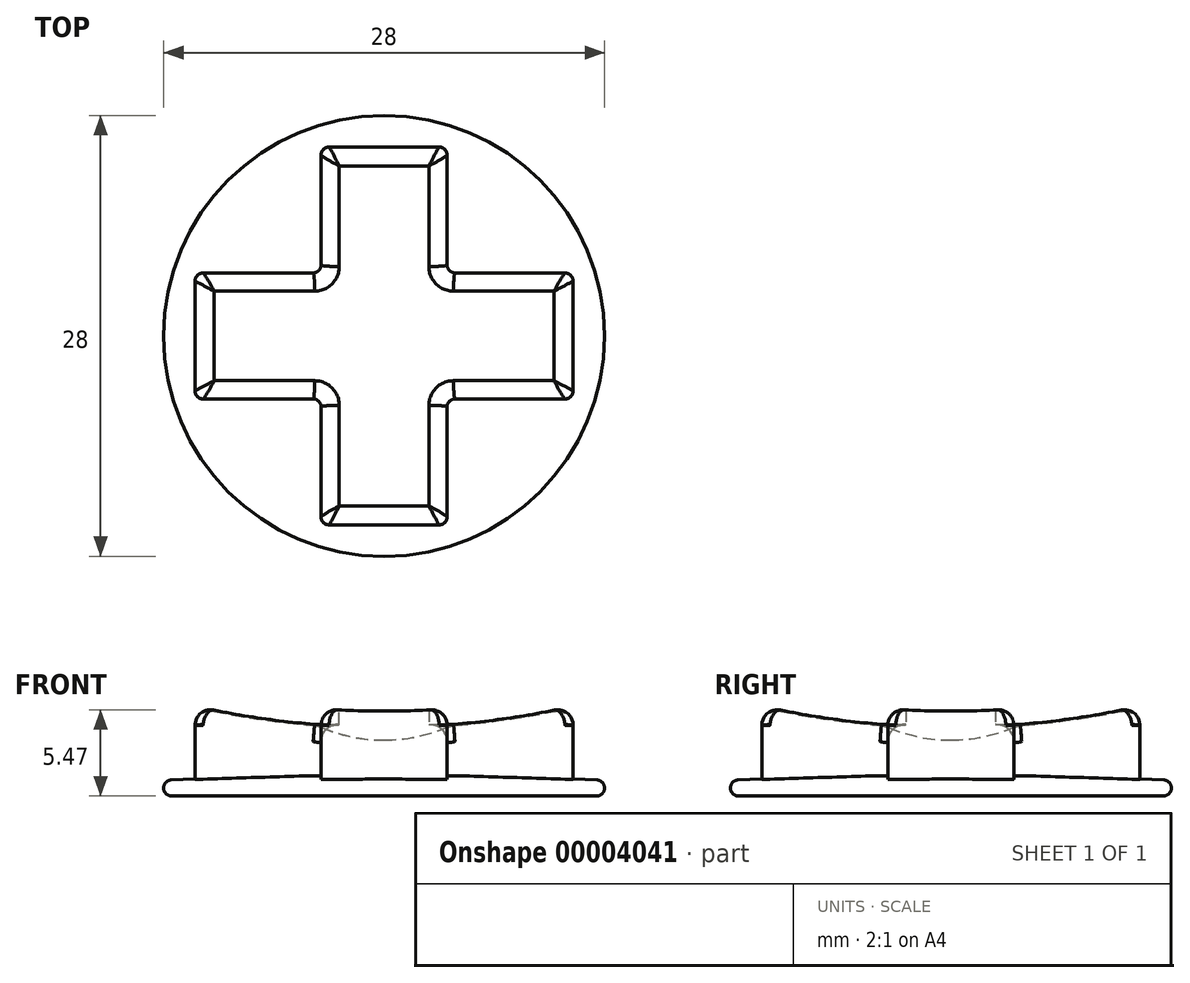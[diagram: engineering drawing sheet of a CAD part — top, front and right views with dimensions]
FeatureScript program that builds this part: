
annotation { "Feature Type Name" : "Feature", "Feature Type Description" : "" }
export const myFeature = defineFeature(function(context is Context, id is Id, definition is map)
    precondition{}
    {
        {
            var Q0;
            Q0=qCreatedBy(makeId("Top.planeOp"),FACE);
            var sketch = newSketch(context, id + "F0", { "sketchPlane" : qUnion([Q0])});
            skCircle(sketch, "E0", {"center": v(0, 0) * mm, "radius": 14 * mm});
            skSolve(sketch);
        }
        {
            var Q0;
            Q0=makeQuery(id+"F0.imprint","IMPRINT",FACE,{"disambiguationData":[TD([[makeQuery(id+"F0.imprint","IMPRINT",EDGE,{"derivedFrom":sQuery(id+"F0.wireOp",EDGE,"E0")}),1.0]])]});
            extrude(context, id + "F1", {"entities" : qUnion([Q0]), "depth" : 1 * mm});
        }
        {
            var Q0;
            Q0=makeQuery(id+"F1.opExtrude","CAP_FACE",FACE,{"disambiguationData":[OSD([sQuery(id+"F0.wireOp",EDGE,"E0")])],"isStart":false});
            var sketch = newSketch(context, id + "F2", { "sketchPlane" : qUnion([Q0])});
            skLineSegment(sketch, "E1", {"start": v(-4, 12) * mm, "end": v(0, 12) * mm});
            skLineSegment(sketch, "E2", {"start": v(0, 12) * mm, "end": v(4, 12) * mm});
            skLineSegment(sketch, "E3", {"start": v(4, 12) * mm, "end": v(4, 4) * mm});
            skLineSegment(sketch, "E4", {"start": v(4, 4) * mm, "end": v(12, 4) * mm});
            skLineSegment(sketch, "E5", {"start": v(12, 4) * mm, "end": v(12, 0) * mm});
            skLineSegment(sketch, "E6", {"start": v(12, 0) * mm, "end": v(12, -4) * mm});
            skLineSegment(sketch, "E7", {"start": v(12, -4) * mm, "end": v(4, -4) * mm});
            skLineSegment(sketch, "E8", {"start": v(4, -12) * mm, "end": v(0, -12) * mm});
            skLineSegment(sketch, "E9", {"start": v(0, -12) * mm, "end": v(-4, -12) * mm});
            skLineSegment(sketch, "E10", {"start": v(-4, -12) * mm, "end": v(-4, -4) * mm});
            skLineSegment(sketch, "E11", {"start": v(-4, -4) * mm, "end": v(-12, -4) * mm});
            skLineSegment(sketch, "E12", {"start": v(-12, -4) * mm, "end": v(-12, 0) * mm});
            skLineSegment(sketch, "E13", {"start": v(-12, 0) * mm, "end": v(-12, 4) * mm});
            skLineSegment(sketch, "E14", {"start": v(-12, 4) * mm, "end": v(-4, 4) * mm});
            skLineSegment(sketch, "E15", {"start": v(-4, 4) * mm, "end": v(-4, 12) * mm});
            skLineSegment(sketch, "E16", {"start": v(-4, 4) * mm, "end": v(0, 0) * mm, "construction": true});
            skLineSegment(sketch, "E17", {"start": v(0, 0) * mm, "end": v(4, 4) * mm, "construction": true});
            skLineSegment(sketch, "E18", {"start": v(0, 0) * mm, "end": v(4, -4) * mm, "construction": true});
            skLineSegment(sketch, "E19", {"start": v(0, 0) * mm, "end": v(-4, -4) * mm, "construction": true});
            skLineSegment(sketch, "E20", {"start": v(4, -4) * mm, "end": v(4, -12) * mm});
            skSolve(sketch);
        }
        {
            var Q0;
            Q0=makeQuery(id+"F2.imprint","IMPRINT",FACE,{"disambiguationData":[TD([[makeQuery(id+"F2.imprint","IMPRINT",EDGE,{"derivedFrom":sQuery(id+"F2.wireOp",EDGE,"E1")}),-1.0]])]});
            extrude(context, id + "F3", {"entities" : qUnion([Q0]), "operationType" : NewBodyOperationType.ADD, "depth" : 4.8 * mm});
        }
        {
            var Q0;
            Q0=qCreatedBy(makeId("Front.planeOp"),FACE);
            var sketch = newSketch(context, id + "F4", { "sketchPlane" : qUnion([Q0])});
            skLineSegment(sketch, "E21", {"start": v(0, 4.3) * mm, "end": v(0, 5.8) * mm});
            skLineSegment(sketch, "E22", {"start": v(0, 5.8) * mm, "end": v(-12.75, 5.8) * mm});
            skArc(sketch, "E23", {"start": v(-12.75, 5.8) * mm, "mid": v(-6.42, 4.68) * mm, "end": v(0, 4.3) * mm});
            skLineSegment(sketch, "E24", {"start": v(0, 4.3) * mm, "end": v(0, 3.55) * mm});
            skLineSegment(sketch, "E25", {"start": v(0, 3.55) * mm, "end": v(0, 0) * mm, "construction": true});
            skArc(sketch, "E26", {"start": v(-4.25, 4.46) * mm, "mid": v(-2.17, 3.78) * mm, "end": v(0, 3.55) * mm});
            skSolve(sketch);
        }
        {
            var Q0;
            {var subQ2=sQuery(id+"F4.wireOp",EDGE,"E21");Q0=makeQuery(id+"F4.imprint","IMPRINT",FACE,{"disambiguationData":[TD([[makeQuery(id+"F4.imprint","IMPRINT",EDGE,{"derivedFrom":subQ2}),1.0]])]});}
            var Q1;
            {var subQ1=sQuery(id+"F4.wireOp",EDGE,"E24");Q1=makeQuery(id+"F4.imprint","IMPRINT",FACE,{"disambiguationData":[TD([[makeQuery(id+"F4.imprint","IMPRINT",EDGE,{"derivedFrom":subQ1}),-1.0]])]});}
            var Q2;
            Q2=sQuery(id+"F4.wireOp",EDGE,"E24");
            revolve(context, id + "F5", {"operationType" : NewBodyOperationType.REMOVE, "entities" : qUnion([Q0, Q1]), "axis" : qUnion([Q2]), "revolveType" : RevolveType.FULL, "oppositeDirection" : true});
        }
        {
            var Q0;
            Q0=qCreatedBy(makeId("Front.planeOp"),FACE);
            var sketch = newSketch(context, id + "F6", { "sketchPlane" : qUnion([Q0])});
            skLineSegment(sketch, "E27.0", {"start": v(-14, 1) * mm, "end": v(14, 1) * mm});
            skLineSegment(sketch, "E28", {"start": v(0, 0) * mm, "end": v(0, 1) * mm, "construction": true});
            skLineSegment(sketch, "E29", {"start": v(0, 1) * mm, "end": v(0, 1.5) * mm});
            skLineSegment(sketch, "E30", {"start": v(0, 1.5) * mm, "end": v(-14, 1) * mm});
            skSolve(sketch);
        }
        {
            var Q0;
            {var subQ1=sQuery(id+"F6.wireOp",EDGE,"E29");Q0=makeQuery(id+"F6.imprint","IMPRINT",FACE,{"disambiguationData":[TD([[makeQuery(id+"F6.imprint","IMPRINT",EDGE,{"derivedFrom":subQ1}),1.0]])]});}
            var Q1;
            Q1=sQuery(id+"F6.wireOp",EDGE,"E29");
            revolve(context, id + "F7", {"operationType" : NewBodyOperationType.ADD, "entities" : qUnion([Q0]), "axis" : qUnion([Q1]), "revolveType" : RevolveType.FULL});
        }
        {
            var Q0;
            Q0=makeQuery(id+"F5.boolean.opBoolean","INTERSECT",EDGE,{"derivedFrom":[makeQuery(id+"F3.opExtrude","SWEPT_FACE",FACE,{"disambiguationData":[OSD([sQuery(id+"F2.wireOp",EDGE,"E8"),sQuery(id+"F2.wireOp",EDGE,"E9")])]}),makeQuery(id+"F5.opRevolve","SWEPT_FACE",FACE,{"disambiguationData":[OSD([sQuery(id+"F4.wireOp",EDGE,"E23")])]})]});
            var Q1;
            Q1=makeQuery(id+"F5.boolean.opBoolean","INTERSECT",EDGE,{"derivedFrom":[makeQuery(id+"F3.opExtrude","SWEPT_FACE",FACE,{"disambiguationData":[OSD([sQuery(id+"F2.wireOp",EDGE,"E12"),sQuery(id+"F2.wireOp",EDGE,"E13")])]}),makeQuery(id+"F5.opRevolve","SWEPT_FACE",FACE,{"disambiguationData":[OSD([sQuery(id+"F4.wireOp",EDGE,"E23")])]})]});
            var Q2;
            Q2=makeQuery(id+"F5.boolean.opBoolean","INTERSECT",EDGE,{"derivedFrom":[makeQuery(id+"F3.opExtrude","SWEPT_FACE",FACE,{"disambiguationData":[OSD([sQuery(id+"F2.wireOp",EDGE,"E5"),sQuery(id+"F2.wireOp",EDGE,"E6")])]}),makeQuery(id+"F5.opRevolve","SWEPT_FACE",FACE,{"disambiguationData":[OSD([sQuery(id+"F4.wireOp",EDGE,"E23")])]})]});
            var Q3;
            Q3=makeQuery(id+"F5.boolean.opBoolean","INTERSECT",EDGE,{"derivedFrom":[makeQuery(id+"F3.opExtrude","SWEPT_FACE",FACE,{"disambiguationData":[OSD([sQuery(id+"F2.wireOp",EDGE,"E1"),sQuery(id+"F2.wireOp",EDGE,"E2")])]}),makeQuery(id+"F5.opRevolve","SWEPT_FACE",FACE,{"disambiguationData":[OSD([sQuery(id+"F4.wireOp",EDGE,"E23")])]})]});
            fillet(context, id + "F8", {"entities" : qUnion([Q0, Q1, Q2, Q3]), "radius" : 1 * mm, "allowEdgeOverflow" : false});
        }
        {
            var Q0;
            Q0=makeQuery(id+"F3.opExtrude","SWEPT_EDGE",EDGE,{"disambiguationData":[OSD([sQuery(id+"F2.wireOp",EDGE,"E3"),sQuery(id+"F2.wireOp",EDGE,"E4")])]});
            var Q1;
            Q1=makeQuery(id+"F3.opExtrude","SWEPT_EDGE",EDGE,{"disambiguationData":[OSD([sQuery(id+"F2.wireOp",EDGE,"E4"),sQuery(id+"F2.wireOp",EDGE,"E5")])]});
            var Q2;
            Q2=makeQuery(id+"F3.opExtrude","SWEPT_EDGE",EDGE,{"disambiguationData":[OSD([sQuery(id+"F2.wireOp",EDGE,"E2"),sQuery(id+"F2.wireOp",EDGE,"E3")])]});
            var Q3;
            Q3=makeQuery(id+"F3.opExtrude","SWEPT_EDGE",EDGE,{"disambiguationData":[OSD([sQuery(id+"F2.wireOp",EDGE,"E1"),sQuery(id+"F2.wireOp",EDGE,"E15")])]});
            var Q4;
            Q4=makeQuery(id+"F3.opExtrude","SWEPT_EDGE",EDGE,{"disambiguationData":[OSD([sQuery(id+"F2.wireOp",EDGE,"E14"),sQuery(id+"F2.wireOp",EDGE,"E15")])]});
            var Q5;
            Q5=makeQuery(id+"F3.opExtrude","SWEPT_EDGE",EDGE,{"disambiguationData":[OSD([sQuery(id+"F2.wireOp",EDGE,"E13"),sQuery(id+"F2.wireOp",EDGE,"E14")])]});
            var Q6;
            Q6=makeQuery(id+"F3.opExtrude","SWEPT_EDGE",EDGE,{"disambiguationData":[OSD([sQuery(id+"F2.wireOp",EDGE,"E11"),sQuery(id+"F2.wireOp",EDGE,"E12")])]});
            var Q7;
            Q7=makeQuery(id+"F3.opExtrude","SWEPT_EDGE",EDGE,{"disambiguationData":[OSD([sQuery(id+"F2.wireOp",EDGE,"E10"),sQuery(id+"F2.wireOp",EDGE,"E11")])]});
            var Q8;
            Q8=makeQuery(id+"F3.opExtrude","SWEPT_EDGE",EDGE,{"disambiguationData":[OSD([sQuery(id+"F2.wireOp",EDGE,"E9"),sQuery(id+"F2.wireOp",EDGE,"E10")])]});
            var Q9;
            Q9=makeQuery(id+"F3.opExtrude","SWEPT_EDGE",EDGE,{"disambiguationData":[OSD([sQuery(id+"F2.wireOp",EDGE,"E8"),sQuery(id+"F2.wireOp",EDGE,"E20")])]});
            var Q10;
            Q10=makeQuery(id+"F3.opExtrude","SWEPT_EDGE",EDGE,{"disambiguationData":[OSD([sQuery(id+"F2.wireOp",EDGE,"E7"),sQuery(id+"F2.wireOp",EDGE,"E20")])]});
            var Q11;
            Q11=makeQuery(id+"F3.opExtrude","SWEPT_EDGE",EDGE,{"disambiguationData":[OSD([sQuery(id+"F2.wireOp",EDGE,"E6"),sQuery(id+"F2.wireOp",EDGE,"E7")])]});
            fillet(context, id + "F9", {"entities" : qUnion([Q0, Q1, Q2, Q3, Q4, Q5, Q6, Q7, Q8, Q9, Q10, Q11]), "radius" : 0.5 * mm, "allowEdgeOverflow" : false});
        }
        {
            var Q0;
            Q0=makeQuery(id+"F5.boolean.opBoolean","COPY",EDGE,{"derivedFrom":makeQuery(id+"F5.opRevolve","SWEPT_EDGE",EDGE,{"disambiguationData":[OSD([sQuery(id+"F4.wireOp",EDGE,"E23"),sQuery(id+"F4.wireOp",EDGE,"E26")])]})});
            fillet(context, id + "F10", {"entities" : qUnion([Q0]), "radius" : 2 * mm, "tangentPropagation" : true, "allowEdgeOverflow" : false});
        }
        {
            var Q0;
            Q0=makeQuery(id+"F11.boolean.opBoolean","MERGE",EDGE,{"derivedFrom":[makeQuery(id+"F1.opExtrude","CAP_EDGE",EDGE,{"disambiguationData":[OSD([sQuery(id+"F0.wireOp",EDGE,"E0")])],"isStart":true}),makeQuery(id+"F11.opRevolve","SWEPT_EDGE",EDGE,{"disambiguationData":[OSD([sQuery(id+"FiIcS1pKXSWZ26h_1.wireOp",EDGE,"75e8e629-aae3-41ac-a448-434de88236d4"),sQuery(id+"FiIcS1pKXSWZ26h_1.wireOp",EDGE,"6a6caec7-bd0c-4301-a166-ca0b6e09a5d0")])]})]});
            var Q1;
            Q1=makeQuery(id+"F11.opRevolve","SWEPT_EDGE",EDGE,{"disambiguationData":[OSD([sQuery(id+"FiIcS1pKXSWZ26h_1.wireOp",EDGE,"6a6caec7-bd0c-4301-a166-ca0b6e09a5d0"),sQuery(id+"FiIcS1pKXSWZ26h_1.wireOp",EDGE,"44006b20-7576-42bf-92f2-3abd5ce75488")])]});
            var Q2;
            Q2=makeQuery(id+"F7.boolean.opBoolean","MERGE",EDGE,{"derivedFrom":[makeQuery(id+"F1.opExtrude","CAP_EDGE",EDGE,{"disambiguationData":[OSD([sQuery(id+"F0.wireOp",EDGE,"E0")])],"isStart":false}),makeQuery(id+"F7.opRevolve","SWEPT_EDGE",EDGE,{"disambiguationData":[OSD([sQuery(id+"F6.wireOp",EDGE,"E27.0"),sQuery(id+"F6.wireOp",EDGE,"E30")])]})]});
            fillet(context, id + "F12", {"entities" : qUnion([Q0, Q1, Q2]), "radius" : .50 * mm, "tangentPropagation" : true, "allowEdgeOverflow" : false});
        }
        {
            var Q0;
            Q0=makeQuery(id+"F5.boolean.opBoolean","INTERSECT",EDGE,{"derivedFrom":[makeQuery(id+"F3.opExtrude","SWEPT_FACE",FACE,{"disambiguationData":[OSD([sQuery(id+"F2.wireOp",EDGE,"E14")])]}),makeQuery(id+"F5.opRevolve","SWEPT_FACE",FACE,{"disambiguationData":[OSD([sQuery(id+"F4.wireOp",EDGE,"E23")])]})]});
            var Q1;
            Q1=makeQuery(id+"F5.boolean.opBoolean","INTERSECT",EDGE,{"derivedFrom":[makeQuery(id+"F3.opExtrude","SWEPT_FACE",FACE,{"disambiguationData":[OSD([sQuery(id+"F2.wireOp",EDGE,"E11")])]}),makeQuery(id+"F5.opRevolve","SWEPT_FACE",FACE,{"disambiguationData":[OSD([sQuery(id+"F4.wireOp",EDGE,"E23")])]})]});
            var Q2;
            Q2=makeQuery(id+"F5.boolean.opBoolean","INTERSECT",EDGE,{"derivedFrom":[makeQuery(id+"F3.opExtrude","SWEPT_FACE",FACE,{"disambiguationData":[OSD([sQuery(id+"F2.wireOp",EDGE,"E10")])]}),makeQuery(id+"F5.opRevolve","SWEPT_FACE",FACE,{"disambiguationData":[OSD([sQuery(id+"F4.wireOp",EDGE,"E23")])]})]});
            var Q3;
            Q3=makeQuery(id+"F5.boolean.opBoolean","INTERSECT",EDGE,{"derivedFrom":[makeQuery(id+"F3.opExtrude","SWEPT_FACE",FACE,{"disambiguationData":[OSD([sQuery(id+"F2.wireOp",EDGE,"E20")])]}),makeQuery(id+"F5.opRevolve","SWEPT_FACE",FACE,{"disambiguationData":[OSD([sQuery(id+"F4.wireOp",EDGE,"E23")])]})]});
            var Q4;
            Q4=makeQuery(id+"F5.boolean.opBoolean","INTERSECT",EDGE,{"derivedFrom":[makeQuery(id+"F3.opExtrude","SWEPT_FACE",FACE,{"disambiguationData":[OSD([sQuery(id+"F2.wireOp",EDGE,"E7")])]}),makeQuery(id+"F5.opRevolve","SWEPT_FACE",FACE,{"disambiguationData":[OSD([sQuery(id+"F4.wireOp",EDGE,"E23")])]})]});
            var Q5;
            Q5=makeQuery(id+"F5.boolean.opBoolean","INTERSECT",EDGE,{"derivedFrom":[makeQuery(id+"F3.opExtrude","SWEPT_FACE",FACE,{"disambiguationData":[OSD([sQuery(id+"F2.wireOp",EDGE,"E3")])]}),makeQuery(id+"F5.opRevolve","SWEPT_FACE",FACE,{"disambiguationData":[OSD([sQuery(id+"F4.wireOp",EDGE,"E23")])]})]});
            var Q6;
            Q6=makeQuery(id+"F5.boolean.opBoolean","INTERSECT",EDGE,{"derivedFrom":[makeQuery(id+"F3.opExtrude","SWEPT_FACE",FACE,{"disambiguationData":[OSD([sQuery(id+"F2.wireOp",EDGE,"E15")])]}),makeQuery(id+"F5.opRevolve","SWEPT_FACE",FACE,{"disambiguationData":[OSD([sQuery(id+"F4.wireOp",EDGE,"E23")])]})]});
            var Q7;
            Q7=makeQuery(id+"F5.boolean.opBoolean","INTERSECT",EDGE,{"derivedFrom":[makeQuery(id+"F3.opExtrude","SWEPT_FACE",FACE,{"disambiguationData":[OSD([sQuery(id+"F2.wireOp",EDGE,"E4")])]}),makeQuery(id+"F5.opRevolve","SWEPT_FACE",FACE,{"disambiguationData":[OSD([sQuery(id+"F4.wireOp",EDGE,"E23")])]})]});
            fillet(context, id + "F13", {"entities" : qUnion([Q0, Q1, Q2, Q3, Q4, Q5, Q6, Q7]), "radius" : 1.1 * mm, "tangentPropagation" : true, "allowEdgeOverflow" : false});
        }
    });
